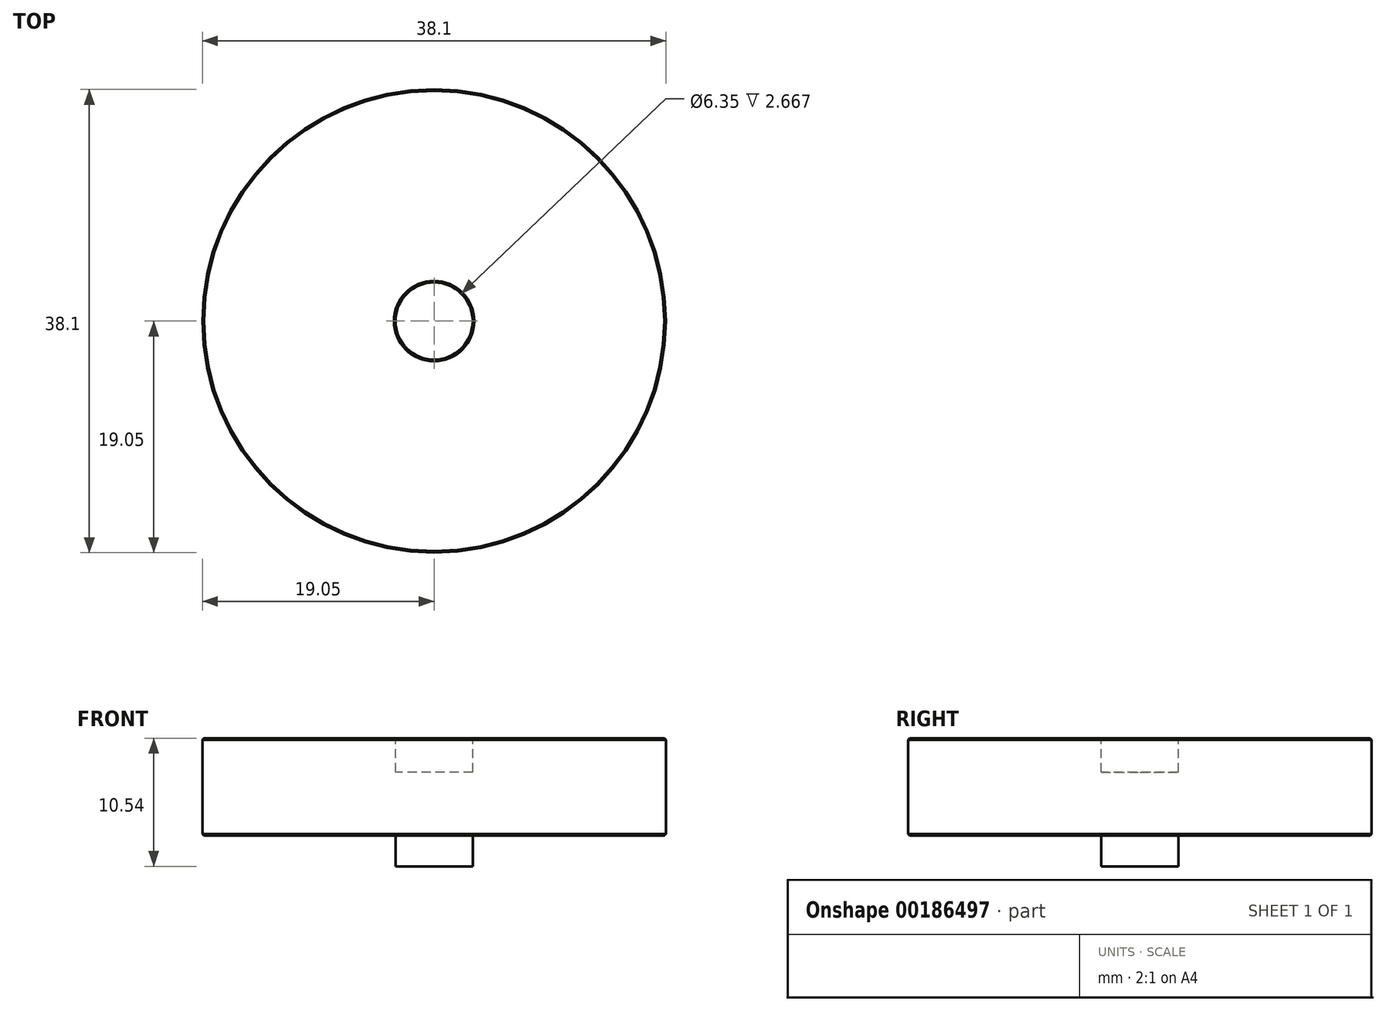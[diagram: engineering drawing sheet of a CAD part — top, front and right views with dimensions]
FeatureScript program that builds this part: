
annotation { "Feature Type Name" : "Feature", "Feature Type Description" : "" }
export const myFeature = defineFeature(function(context is Context, id is Id, definition is map)
    precondition{}
    {
        {
            var Q0;
            Q0=qCreatedBy(makeId("Right.planeOp"),FACE);
            var sketch = newSketch(context, id + "F0", { "sketchPlane" : qUnion([Q0])});
            skLineSegment(sketch, "E0", {"start": v(0, -2.54) * mm, "end": v(-3.18, -2.54) * mm});
            skLineSegment(sketch, "E1", {"start": v(-3.18, -2.54) * mm, "end": v(-3.18, 0) * mm});
            skLineSegment(sketch, "E2", {"start": v(-3.18, 0) * mm, "end": v(-19.05, 0) * mm});
            skLineSegment(sketch, "E3", {"start": v(-19.05, 0) * mm, "end": v(-19.05, 8) * mm});
            skLineSegment(sketch, "E4", {"start": v(-19.05, 8) * mm, "end": v(-3.18, 8) * mm});
            skLineSegment(sketch, "E5", {"start": v(-3.18, 8) * mm, "end": v(-3.18, 5.2) * mm});
            skLineSegment(sketch, "E6", {"start": v(-3.18, 5.2) * mm, "end": v(0, 5.2) * mm});
            skLineSegment(sketch, "E7", {"start": v(0, 5.2) * mm, "end": v(0, 0) * mm});
            skLineSegment(sketch, "E8", {"start": v(0, 0) * mm, "end": v(0, -2.54) * mm});
            skSolve(sketch);
        }
        {
            var Q0;
            Q0 = qSketchRegion(id + "F0", true);
            var Q1;
            Q1=sQuery(id+"F0.wireOp",EDGE,"E7");
            revolve(context, id + "F1", {"entities" : qUnion([Q0]), "axis" : qUnion([Q1]), "revolveType" : RevolveType.FULL});
        }
        {
            var Q0;
            Q0=makeQuery(id+"F1.opRevolve","SWEPT_EDGE",EDGE,{"disambiguationData":[OSD([sQuery(id+"F0.wireOp",EDGE,"E1"),sQuery(id+"F0.wireOp",EDGE,"E2")])]});
            fillet(context, id + "F2", {"entities" : qUnion([Q0]), "radius" : 0.05 * mm, "tangentPropagation" : true, "allowEdgeOverflow" : false});
        }
        {
            var Q0;
            Q0=makeQuery(id+"F1.opRevolve","SWEPT_EDGE",EDGE,{"disambiguationData":[OSD([sQuery(id+"F0.wireOp",EDGE,"E2"),sQuery(id+"F0.wireOp",EDGE,"E3")])]});
            var Q1;
            Q1=makeQuery(id+"F1.opRevolve","SWEPT_EDGE",EDGE,{"disambiguationData":[OSD([sQuery(id+"F0.wireOp",EDGE,"E3"),sQuery(id+"F0.wireOp",EDGE,"E4")])]});
            var Q2;
            Q2=makeQuery(id+"F1.opRevolve","SWEPT_EDGE",EDGE,{"disambiguationData":[OSD([sQuery(id+"F0.wireOp",EDGE,"E4"),sQuery(id+"F0.wireOp",EDGE,"E5")])]});
            chamfer(context, id + "F3", {"entities" : qUnion([Q0, Q1, Q2]), "width" : 0.13 * mm, "tangentPropagation" : true});
        }
    });
